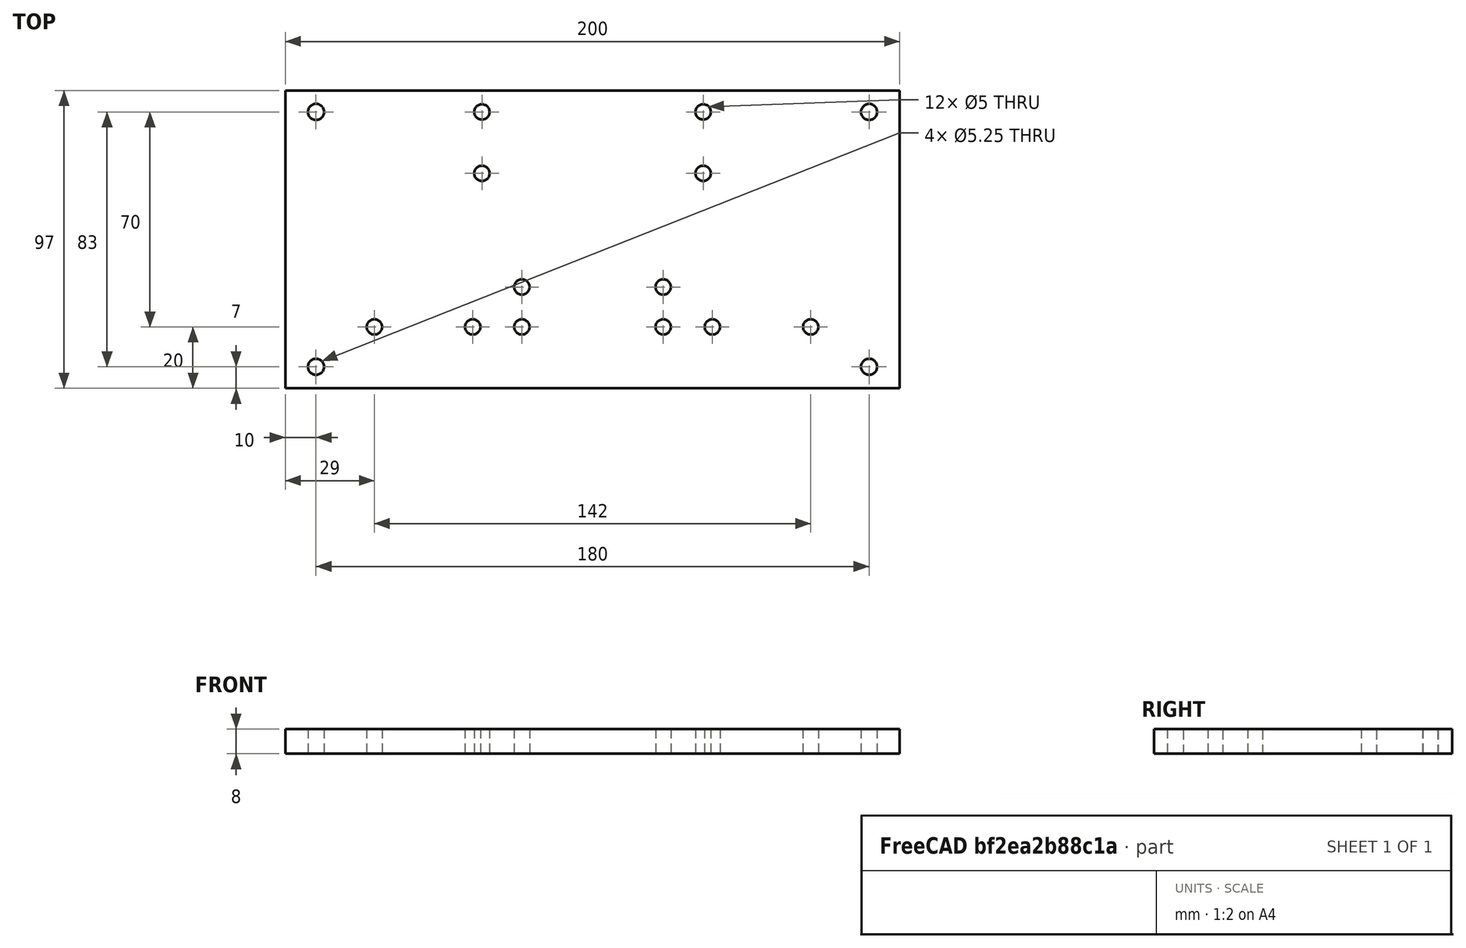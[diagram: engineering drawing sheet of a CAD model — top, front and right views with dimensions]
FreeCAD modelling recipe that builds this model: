
FCSTD DOCUMENT  (FreeCAD 0.15R4671 (Git))
Label: base-right
License: All rights reserved
LicenseURL: http://en.wikipedia.org/wiki/All_rights_reserved
objects: Drawing::FeatureView×27, Drawing::FeatureViewPart×2, Sketcher::SketchObject×1, PartDesign::Pad×1, Drawing::FeaturePage×1
note: 3 computed .brp shape members not serialized (recipe doc carries the construction recipe); baked Part::Feature solids carry a one-line shape summary decoded from their .brp

FEATURE [Sketcher::SketchObject] Sketch  label="main-sketch"
  Placement = pos=(0,0,0) rot=(0,0,1;1.5708rad)
  sketch-geometry (42):
    g0: LineSegment StartX=-48.5 StartY=100 StartZ=0 EndX=48.5 EndY=100 EndZ=0
    g1: LineSegment StartX=48.5 StartY=100 StartZ=0 EndX=48.5 EndY=-100 EndZ=0
    g2: LineSegment StartX=48.5 StartY=-100 StartZ=0 EndX=-48.5 EndY=-100 EndZ=0
    g3: LineSegment StartX=-48.5 StartY=-100 StartZ=0 EndX=-48.5 EndY=100 EndZ=0
    g4: LineSegment [constr] StartX=-28.5 StartY=100 StartZ=0 EndX=-28.5 EndY=-100 EndZ=0
    g5: LineSegment [constr] StartX=-15.5 StartY=23 StartZ=0 EndX=-15.5 EndY=-23 EndZ=0
    g6: LineSegment [constr] StartX=-28.5 StartY=23 StartZ=0 EndX=-15.5 EndY=23 EndZ=0
    g7: LineSegment [constr] StartX=-15.5 StartY=-23 StartZ=0 EndX=-28.5 EndY=-23 EndZ=0
    g8: Circle CenterX=-28.5 CenterY=71 CenterZ=0 NormalX=0 NormalY=0 NormalZ=1 Radius=2.5
    g9: Circle CenterX=-28.5 CenterY=39 CenterZ=0 NormalX=0 NormalY=0 NormalZ=1 Radius=2.5
    g10: Circle CenterX=-28.5 CenterY=-39 CenterZ=0 NormalX=0 NormalY=0 NormalZ=1 Radius=2.5
    g11: Circle CenterX=-28.5 CenterY=-71 CenterZ=0 NormalX=0 NormalY=0 NormalZ=1 Radius=2.5
    g12: GeomPoint [constr] X=-28.5 Y=34 Z=0
    g13: GeomPoint [constr] X=-28.5 Y=30 Z=0
    g14: Circle CenterX=-28.5 CenterY=23 CenterZ=0 NormalX=0 NormalY=0 NormalZ=1 Radius=2.5
    g15: Circle CenterX=-15.5 CenterY=23 CenterZ=0 NormalX=0 NormalY=0 NormalZ=1 Radius=2.5
    g16: Circle CenterX=-28.5 CenterY=-23 CenterZ=0 NormalX=0 NormalY=0 NormalZ=1 Radius=2.5
    g17: Circle CenterX=-15.5 CenterY=-23 CenterZ=0 NormalX=0 NormalY=0 NormalZ=1 Radius=2.5
    g18: LineSegment [constr] StartX=-41.5 StartY=90 StartZ=0 EndX=41.5 EndY=90 EndZ=0
    g19: LineSegment [constr] StartX=41.5 StartY=90 StartZ=0 EndX=41.5 EndY=-90 EndZ=0
    g20: LineSegment [constr] StartX=41.5 StartY=-90 StartZ=0 EndX=-41.5 EndY=-90 EndZ=0
    g21: LineSegment [constr] StartX=-41.5 StartY=-90 StartZ=0 EndX=-41.5 EndY=90 EndZ=0
    g22: Circle CenterX=-41.5 CenterY=90 CenterZ=0 NormalX=0 NormalY=0 NormalZ=1 Radius=2.625
    g23: Circle CenterX=41.5 CenterY=90 CenterZ=0 NormalX=0 NormalY=0 NormalZ=1 Radius=2.625
    g24: Circle CenterX=-41.5 CenterY=-90 CenterZ=0 NormalX=0 NormalY=0 NormalZ=1 Radius=2.625
    g25: Circle CenterX=41.5 CenterY=-90 CenterZ=0 NormalX=0 NormalY=0 NormalZ=1 Radius=2.625
    g26: GeomPoint [constr] X=18.5 Y=0 Z=0
    g27: GeomPoint [constr] X=22.5 Y=0 Z=0
    g28: GeomPoint [constr] X=46.5 Y=0 Z=0
    g29: GeomPoint [constr] X=41.5 Y=0 Z=0
    g30: LineSegment [constr] StartX=21.5 StartY=36 StartZ=0 EndX=41.5 EndY=36 EndZ=0
    g31: LineSegment [constr] StartX=41.5 StartY=36 StartZ=0 EndX=41.5 EndY=-36 EndZ=0
    g32: LineSegment [constr] StartX=41.5 StartY=-36 StartZ=0 EndX=21.5 EndY=-36 EndZ=0
    g33: LineSegment [constr] StartX=21.5 StartY=-36 StartZ=0 EndX=21.5 EndY=36 EndZ=0
    g34: Circle CenterX=21.5 CenterY=36 CenterZ=0 NormalX=0 NormalY=0 NormalZ=1 Radius=2.5
    g35: Circle CenterX=41.5 CenterY=36 CenterZ=0 NormalX=0 NormalY=0 NormalZ=1 Radius=2.5
    g36: Circle CenterX=21.5 CenterY=-36 CenterZ=0 NormalX=0 NormalY=0 NormalZ=1 Radius=2.5
    g37: Circle CenterX=41.5 CenterY=-36 CenterZ=0 NormalX=0 NormalY=0 NormalZ=1 Radius=2.5
    g38: GeomPoint [constr] X=-35.5 Y=0 Z=0
    g39: GeomPoint [constr] X=-28.5 Y=0 Z=0
    g40: GeomPoint [constr] X=-28.5 Y=55 Z=0
    g41: GeomPoint [constr] X=-28.5 Y=-55 Z=0
  constraints (103):
    c: Coincident(g0,g1)
    c: Coincident(g1,g2)
    c: Coincident(g2,g3)
    c: Coincident(g3,g0)
    c: Horizontal(g0)
    c: Horizontal(g2)
    c: Vertical(g1)
    c: Vertical(g3)
    c: DistanceY(g0,g1) = -200
    c: Symmetric(g0,g1,g-1)
    c: Symmetric(g4,g4,g-1)
    c: Vertical(g5)
    c: Symmetric(g5,g5,g-1)
    c: PointOnObject(g6,g4)
    c: Coincident(g6,g5)
    c: Horizontal(g6)
    c: Coincident(g7,g5)
    c: PointOnObject(g7,g4)
    c: Horizontal(g7)
    c: DistanceX(g7,g5) = 13
    c: DistanceY(g5,g5) = -46
    c: DistanceX(g2,g4) = 20
    c: PointOnObject(g8,g4)
    c: PointOnObject(g11,g4)
    c: Radius(g10) = 2.5
    c: Equal(g10,g11)
    c: Equal(g10,g9)
    c: Equal(g10,g8)
    c: DistanceY(g8,g9) = -32
    c: DistanceY(g10,g11) = -32
    c: Symmetric(g9,g10,g-1)
    c: PointOnObject(g4,g0)
    c: PointOnObject(g12,g4)
    c: DistanceY(g9,g12) = -5
    c: PointOnObject(g13,g4)
    c: DistanceY(g13,g6) = -7
    c: DistanceY(g12,g13) = -4
    c: Coincident(g14,g6)
    c: Coincident(g15,g5)
    c: Coincident(g16,g7)
    c: Coincident(g17,g5)
    c: Radius(g14) = 2.5
    c: Equal(g14,g15)
    c: Equal(g14,g17)
    c: Equal(g14,g16)
    c: Coincident(g18,g19)
    c: Coincident(g19,g20)
    c: Coincident(g20,g21)
    c: Coincident(g21,g18)
    c: Horizontal(g18)
    c: Horizontal(g20)
    c: Vertical(g19)
    c: Vertical(g21)
    c: DistanceX(g18,g0) = -7
    c: DistanceY(g18,g0) = 10
    c: Symmetric(g0,g0,g-2)
    c: Symmetric(g18,g18,g-2)
    c: Symmetric(g18,g19,g-1)
    c: Coincident(g22,g18)
    c: Coincident(g23,g18)
    c: Coincident(g24,g20)
    c: Coincident(g25,g19)
    c: Radius(g25) = 2.625
    c: Equal(g25,g24)
    c: Equal(g25,g22)
    c: Equal(g25,g23)
    c: PointOnObject(g26,g-1)
    c: PointOnObject(g27,g-1)
    c: DistanceX(g26,g27) = 4
    c: PointOnObject(g28,g-1)
    c: DistanceX(g27,g28) = 24
    c: PointOnObject(g29,g-1)
    c: DistanceX(g29,g28) = 5
    c: Coincident(g30,g31)
    c: Coincident(g31,g32)
    c: Coincident(g32,g33)
    c: Coincident(g33,g30)
    c: Horizontal(g30)
    c: Horizontal(g32)
    c: Vertical(g31)
    c: Vertical(g33)
    c: PointOnObject(g29,g31)
    c: DistanceX(g30,g30) = -20
    c: DistanceY(g30,g31) = -72
    c: Symmetric(g30,g32,g-1)
    c: Coincident(g34,g30)
    c: Coincident(g35,g30)
    c: Coincident(g36,g32)
    c: Coincident(g37,g31)
    c: Radius(g37) = 2.5
    c: Equal(g37,g36)
    c: Equal(g37,g34)
    c: Equal(g37,g35)
    c: PointOnObject(g31,g19)
    c: PointOnObject(g38,g-1)
    c: PointOnObject(g39,g4)
    c: PointOnObject(g39,g-1)
    c: DistanceX(g38,g39) = 7
    c: DistanceX(g26,g38) = -54
    c: PointOnObject(g40,g4)
    c: Symmetric(g8,g9,g40)
    c: PointOnObject(g41,g4)
    c: Symmetric(g10,g11,g41)
FEATURE [PartDesign::Pad] Pad  label="base-right"
  Length = 8
  Length2 = 100
  Placement = pos=(0,0,0) rot=(0,0,1;1.5708rad)
  Sketch = -> Sketch
  Type = 0
FEATURE [Drawing::FeatureViewPart] Ortho  label="Ortho_0_0"
  Direction = (0,0,1)
  HiddenWidth = 0.15
  LineWidth = 0.35
  Rotation = 0
  ShowHiddenLines = false
  ShowSmoothLines = false
  Source = -> Pad
  Tolerance = 0.05
  ViewResult = <g id="Ortho_0_0"\n   transform="rotate(0,148.5,84.1667) translate(148.5,84.1667) scale(1,1)"\n  >\n<g   stroke="rgb(0, 0, 0)"\n   stroke-width="0.35"\n   stroke-linecap="butt"\n   stroke-linejoin="miter"\n   fill="none"\n   transform="scale(1,-1)"\n  >\n<path id= "1" d=" M -100 -48.5 L -100 48.5 " />\n<path id= "2" d=" M -100 48.5 L 100 48.5 " />\n<path id= "3" d=" M 100 48.5 L 100 -48.5 " />\n<path id= "4" d=" M 100 -48.5 L -100 -48.5 " />\n<circle cx ="90" cy ="41.5" r ="2.625" /><circle cx ="90" cy ="-41.5" r ="2.625" /><circle cx ="-90" cy ="41.5" r ="2.625" /><circle cx ="-90" cy ="-41.5" r ="2.625" /><circle cx ="36" cy ="41.5" r ="2.5" /><circle cx ="-36" cy ="41.5" r ="2.5" /><circle cx ="-39" cy ="-28.5" r ="2.5" /><circle cx ="39" cy ="-28.5" r ="2.5" /><circle cx ="71" cy ="-28.5" r ="2.5" /><circle cx ="-36" cy ="21.5" r ="2.5" /><circle cx ="36" cy ="21.5" r ="2.5" /><circle cx ="-71" cy ="-28.5" r ="2.5" /><circle cx ="-23" cy ="-15.5" r ="2.5" /><circle cx ="23" cy ="-15.5" r ="2.5" /><circle cx ="-23" cy ="-28.5" r ="2.5" /><circle cx ="23" cy ="-28.5" r ="2.5" /></g>\n</g>
  Visible = true
  X = 148.5
  Y = 84.1667
FEATURE [Drawing::FeatureViewPart] Ortho001  label="Ortho_0_-1"
  Direction = (0,-1,0)
  HiddenWidth = 0.15
  LineWidth = 0.35
  Rotation = 90
  ShowHiddenLines = false
  ShowSmoothLines = false
  Source = -> Pad
  Tolerance = 0.05
  ViewResult = <g id="Ortho_0_-1"\n   transform="rotate(90,148.5,174.333) translate(148.5,174.333) scale(1,1)"\n  >\n<g   stroke="rgb(0, 0, 0)"\n   stroke-width="0.35"\n   stroke-linecap="butt"\n   stroke-linejoin="miter"\n   fill="none"\n   transform="scale(1,-1)"\n  >\n<path id= "1" d=" M 0 -100 L -8 -100 " />\n<path id= "2" d=" M 0 100 L -8 100 " />\n<path id= "3" d=" M 0 100 L 0 -100 " />\n<path id= "4" d=" M -8 100 L -8 -100 " />\n</g>\n</g>
  Visible = true
  X = 148.5
  Y = 174.333
FEATURE [Drawing::FeatureView] dim001
  Rotation = 0
  ViewResult = <g> \n  <line x1="46.500000" y1="35.666700" x2="20.569600" y2="35.666700" style="stroke:rgb(0,0,255);stroke-width:0.50" />\n<line x1="46.500000" y1="132.666700" x2="20.569600" y2="132.666700" style="stroke:rgb(0,0,255);stroke-width:0.50" />\n<line x1="21.569600" y1="35.666700" x2="21.569600" y2="132.666700" style="stroke:rgb(0,0,255);stroke-width:0.50" /> \n  <polygon points="21.569600,132.666700 22.569600,129.666700 21.569600,128.666700 20.569600,129.666700" style="fill:rgb(0,0,255);stroke:rgb(0,0,255);stroke-width:0" /><polygon points="21.569600,35.666700 20.569600,38.666700 21.569600,39.666700 22.569600,38.666700" style="fill:rgb(0,0,255);stroke:rgb(0,0,255);stroke-width:0" /> \n  <text x="19.569600" y="84.166700" font-family="inherit" font-size="3.6" fill="rgb(0,0,255)" text-anchor="middle" transform="rotate(-90.000000 19.569600,84.166700)" >97</text> </g>
  Visible = true
  X = 0
  Y = 0
FEATURE [Drawing::FeatureView] dim002
  Rotation = 0
  ViewResult = <g> \n  <line x1="56.500000" y1="42.666700" x2="30.059043" y2="42.666700" style="stroke:rgb(0,0,255);stroke-width:0.50" />\n<line x1="56.500000" y1="125.666700" x2="30.059043" y2="125.666700" style="stroke:rgb(0,0,255);stroke-width:0.50" />\n<line x1="31.059043" y1="42.666700" x2="31.059043" y2="125.666700" style="stroke:rgb(0,0,255);stroke-width:0.50" /> \n  <polygon points="31.059043,125.666700 32.059043,122.666700 31.059043,121.666700 30.059043,122.666700" style="fill:rgb(0,0,255);stroke:rgb(0,0,255);stroke-width:0" /><polygon points="31.059043,42.666700 30.059043,45.666700 31.059043,46.666700 32.059043,45.666700" style="fill:rgb(0,0,255);stroke:rgb(0,0,255);stroke-width:0" /> \n  <text x="29.059043" y="84.166700" font-family="inherit" font-size="3.6" fill="rgb(0,0,255)" text-anchor="middle" transform="rotate(-90.000000 29.059043,84.166700)" >83</text> </g>
  Visible = true
  X = 0
  Y = 0
FEATURE [Drawing::FeatureView] dim003
  Rotation = 0
  ViewResult = <g> \n  <line x1="48.500000" y1="33.666700" x2="48.500000" y2="9.255344" style="stroke:rgb(0,0,255);stroke-width:0.50" />\n<line x1="248.500000" y1="33.666700" x2="248.500000" y2="9.255344" style="stroke:rgb(0,0,255);stroke-width:0.50" />\n<line x1="48.500000" y1="10.255344" x2="248.500000" y2="10.255344" style="stroke:rgb(0,0,255);stroke-width:0.50" /> \n  <polygon points="248.500000,10.255344 245.500000,9.255344 244.500000,10.255344 245.500000,11.255344" style="fill:rgb(0,0,255);stroke:rgb(0,0,255);stroke-width:0" /><polygon points="48.500000,10.255344 51.500000,11.255344 52.500000,10.255344 51.500000,9.255344" style="fill:rgb(0,0,255);stroke:rgb(0,0,255);stroke-width:0" /> \n  <text x="148.500000" y="8.255344" font-family="inherit" font-size="3.6" fill="rgb(0,0,255)" text-anchor="middle" transform="rotate(0.000000 148.500000,8.255344)" >200</text> </g>
  Visible = true
  X = 0
  Y = 0
FEATURE [Drawing::FeatureView] dim004
  Rotation = 0
  ViewResult = <g> \n  <line x1="58.500000" y1="40.666700" x2="58.500000" y2="17.873400" style="stroke:rgb(0,0,255);stroke-width:0.50" />\n<line x1="238.500000" y1="40.666700" x2="238.500000" y2="17.873400" style="stroke:rgb(0,0,255);stroke-width:0.50" />\n<line x1="58.500000" y1="18.873400" x2="238.500000" y2="18.873400" style="stroke:rgb(0,0,255);stroke-width:0.50" /> \n  <polygon points="238.500000,18.873400 235.500000,17.873400 234.500000,18.873400 235.500000,19.873400" style="fill:rgb(0,0,255);stroke:rgb(0,0,255);stroke-width:0" /><polygon points="58.500000,18.873400 61.500000,19.873400 62.500000,18.873400 61.500000,17.873400" style="fill:rgb(0,0,255);stroke:rgb(0,0,255);stroke-width:0" /> \n  <text x="148.500000" y="16.873400" font-family="inherit" font-size="3.6" fill="rgb(0,0,255)" text-anchor="middle" transform="rotate(0.000000 148.500000,16.873400)" >180</text> </g>
  Visible = true
  X = 0
  Y = 0
FEATURE [Drawing::FeatureView] dim009
  Rotation = 0
  ViewResult = <g> \n  <line x1="123.500000" y1="99.666700" x2="117.888672" y2="99.666700" style="stroke:rgb(0,0,255);stroke-width:0.50" />\n<line x1="123.500000" y1="112.666700" x2="117.888672" y2="112.666700" style="stroke:rgb(0,0,255);stroke-width:0.50" />\n<line x1="118.888672" y1="99.666700" x2="118.888672" y2="112.666700" style="stroke:rgb(0,0,255);stroke-width:0.50" /> \n  <polygon points="118.888672,112.666700 119.888672,109.666700 118.888672,108.666700 117.888672,109.666700" style="fill:rgb(0,0,255);stroke:rgb(0,0,255);stroke-width:0" /><polygon points="118.888672,99.666700 117.888672,102.666700 118.888672,103.666700 119.888672,102.666700" style="fill:rgb(0,0,255);stroke:rgb(0,0,255);stroke-width:0" /> \n  <text x="116.888672" y="106.166700" font-family="inherit" font-size="3.6" fill="rgb(0,0,255)" text-anchor="middle" transform="rotate(-90.000000 116.888672,106.166700)" >13</text> </g>
  Visible = true
  X = 0
  Y = 0
FEATURE [Drawing::FeatureView] dim012
  Rotation = 0
  ViewResult = <g> \n  <line x1="110.500000" y1="42.666700" x2="92.685148" y2="42.666700" style="stroke:rgb(0,0,255);stroke-width:0.50" />\n<line x1="110.500000" y1="62.666700" x2="92.685148" y2="62.666700" style="stroke:rgb(0,0,255);stroke-width:0.50" />\n<line x1="93.685148" y1="42.666700" x2="93.685148" y2="62.666700" style="stroke:rgb(0,0,255);stroke-width:0.50" /> \n  <polygon points="93.685148,62.666700 94.685148,59.666700 93.685148,58.666700 92.685148,59.666700" style="fill:rgb(0,0,255);stroke:rgb(0,0,255);stroke-width:0" /><polygon points="93.685148,42.666700 92.685148,45.666700 93.685148,46.666700 94.685148,45.666700" style="fill:rgb(0,0,255);stroke:rgb(0,0,255);stroke-width:0" /> \n  <text x="91.685148" y="52.666700" font-family="inherit" font-size="3.6" fill="rgb(0,0,255)" text-anchor="middle" transform="rotate(-90.000000 91.685148,52.666700)" >20</text> </g>
  Visible = true
  X = 0
  Y = 0
FEATURE [Drawing::FeatureView] centerLines001
  Rotation = 0
  ViewResult = <g transform="scale(1.000000,1.000000)" stroke="rgb(0,0,255)"  stroke-width="0.320000" > <path d="M 148.500000,35.666700 L 148.500000,38.666700 M 148.500000,40.666700 L 148.500000,46.666700 M 148.500000,48.666700 L 148.500000,51.666700 M 148.500000,53.666700 L 148.500000,59.666700 M 148.500000,61.666700 L 148.500000,64.666700 M 148.500000,66.666700 L 148.500000,72.666700 M 148.500000,74.666700 L 148.500000,77.666700 M 148.500000,79.666700 L 148.500000,85.666700 M 148.500000,87.666700 L 148.500000,90.666700 M 148.500000,92.666700 L 148.500000,98.666700 M 148.500000,100.666700 L 148.500000,103.666700 M 148.500000,105.666700 L 148.500000,111.666700 M 148.500000,113.666700 L 148.500000,116.666700 M 148.500000,118.666700 L 148.500000,124.666700 M 148.500000,126.666700 L 148.500000,129.666700 M 148.500000,131.666700 L 148.500000,134.315710 "/>\n<path d="M 148.500000,35.666700 L 148.500000,38.666700 M 148.500000,40.666700 L 148.500000,46.666700 M 148.500000,48.666700 L 148.500000,51.666700 M 148.500000,53.666700 L 148.500000,59.666700 M 148.500000,61.666700 L 148.500000,64.666700 M 148.500000,66.666700 L 148.500000,72.666700 M 148.500000,74.666700 L 148.500000,77.666700 M 148.500000,79.666700 L 148.500000,85.666700 M 148.500000,87.666700 L 148.500000,90.666700 M 148.500000,92.666700 L 148.500000,98.666700 M 148.500000,100.666700 L 148.500000,103.666700 M 148.500000,105.666700 L 148.500000,111.666700 M 148.500000,113.666700 L 148.500000,116.666700 M 148.500000,118.666700 L 148.500000,124.666700 M 148.500000,126.666700 L 148.500000,129.666700 M 148.500000,131.666700 L 148.500000,134.315710 "/> </g> 
  Visible = true
  X = 0
  Y = 0
FEATURE [Drawing::FeatureView] dim015
  Rotation = 0
  ViewResult = <g>  <circle cx ="77.500000" cy ="112.666700" r="0.250000" stroke="none" fill="rgb(0,0,255)" /> \n<line x1="81.248488" y1="106.813745" x2="76.151703" y2="114.771954" style="stroke:rgb(0,0,255);stroke-width:0.50" />\n<polygon points="78.848297,110.561446 81.308355,108.574459 81.005572,107.193039 79.624151,107.495822" style="fill:rgb(0,0,255);stroke:rgb(0,0,255);stroke-width:0" />\n<polygon points="76.151703,114.771954 73.691645,116.758941 73.994428,118.140361 75.375849,117.837578" style="fill:rgb(0,0,255);stroke:rgb(0,0,255);stroke-width:0" />\n<line x1="81.248488" y1="106.813745" x2="91.054340" y2="106.813745" style="stroke:rgb(0,0,255);stroke-width:0.50" />\n<text x="86.151414" y="104.813745" font-family="inherit" font-size="3.6" fill="rgb(0,0,255)" text-anchor="middle"  >2 x Ø5</text> </g>
  Visible = true
  X = 0
  Y = 0
FEATURE [Drawing::FeatureView] dim016
  Rotation = 0
  ViewResult = <g>  <circle cx ="187.500000" cy ="112.666700" r="0.250000" stroke="none" fill="rgb(0,0,255)" /> \n<line x1="192.264741" y1="106.113327" x2="186.029843" y2="114.688738" style="stroke:rgb(0,0,255);stroke-width:0.50" />\n<polygon points="188.970157,110.644662 191.543161,108.806279 191.322409,107.409401 189.925530,107.630153" style="fill:rgb(0,0,255);stroke:rgb(0,0,255);stroke-width:0" />\n<polygon points="186.029843,114.688738 183.456839,116.527121 183.677591,117.923999 185.074470,117.703247" style="fill:rgb(0,0,255);stroke:rgb(0,0,255);stroke-width:0" />\n<line x1="192.264741" y1="106.113327" x2="202.771011" y2="106.113327" style="stroke:rgb(0,0,255);stroke-width:0.50" />\n<text x="197.517876" y="104.113327" font-family="inherit" font-size="3.6" fill="rgb(0,0,255)" text-anchor="middle"  >2 x Ø5</text> </g>
  Visible = true
  X = 0
  Y = 0
FEATURE [Drawing::FeatureView] dim017
  Rotation = 0
  ViewResult = <g>  <circle cx ="125.500000" cy ="112.666700" r="0.250000" stroke="none" fill="rgb(0,0,255)" /> \n<line x1="129.227121" y1="106.813745" x2="124.157167" y2="114.775443" style="stroke:rgb(0,0,255);stroke-width:0.50" />\n<polygon points="126.842833,110.557957 129.297730,108.564598 128.991366,107.183967 127.610736,107.490331" style="fill:rgb(0,0,255);stroke:rgb(0,0,255);stroke-width:0" />\n<polygon points="124.157167,114.775443 121.702270,116.768802 122.008634,118.149433 123.389264,117.843069" style="fill:rgb(0,0,255);stroke:rgb(0,0,255);stroke-width:0" />\n<line x1="129.227121" y1="106.813745" x2="141.484436" y2="106.813745" style="stroke:rgb(0,0,255);stroke-width:0.50" />\n<text x="135.355779" y="104.813745" font-family="inherit" font-size="3.6" fill="rgb(0,0,255)" text-anchor="middle"  >4 x Ø5</text> </g>
  Visible = true
  X = 0
  Y = 0
FEATURE [Drawing::FeatureView] dim018
  Rotation = 0
  ViewResult = <g>  <circle cx ="112.500000" cy ="62.666700" r="0.250000" stroke="none" fill="rgb(0,0,255)" /> \n<line x1="115.919179" y1="56.733858" x2="111.251684" y2="64.832735" style="stroke:rgb(0,0,255);stroke-width:0.50" />\n<polygon points="113.748316,60.500665 116.112709,58.400750 115.745621,57.035009 114.379881,57.402097" style="fill:rgb(0,0,255);stroke:rgb(0,0,255);stroke-width:0" />\n<polygon points="111.251684,64.832735 108.887291,66.932650 109.254379,68.298391 110.620119,67.931303" style="fill:rgb(0,0,255);stroke:rgb(0,0,255);stroke-width:0" />\n<line x1="115.919179" y1="56.733858" x2="127.125867" y2="56.733858" style="stroke:rgb(0,0,255);stroke-width:0.50" />\n<text x="121.522523" y="54.733858" font-family="inherit" font-size="3.6" fill="rgb(0,0,255)" text-anchor="middle"  >4 x Ø5</text> </g>
  Visible = true
  X = 0
  Y = 0
FEATURE [Drawing::FeatureView] centerLines002
  Rotation = 0
  ViewResult = <blob: 3032 chars omitted>
  Visible = true
  X = 0
  Y = 0
FEATURE [Drawing::FeatureView] dim005
  Rotation = 0
  ViewResult = <g> \n  <line x1="46.500000" y1="166.333000" x2="33.031552" y2="166.333000" style="stroke:rgb(0,0,255);stroke-width:0.50" />\n<line x1="46.500000" y1="174.333000" x2="33.031552" y2="174.333000" style="stroke:rgb(0,0,255);stroke-width:0.50" />\n<line x1="34.031552" y1="166.333000" x2="34.031552" y2="174.333000" style="stroke:rgb(0,0,255);stroke-width:0.50" /> \n  <polygon points="34.031552,174.333000 33.031552,177.333000 34.031552,178.333000 35.031552,177.333000" style="fill:rgb(0,0,255);stroke:rgb(0,0,255);stroke-width:0" /><polygon points="34.031552,166.333000 35.031552,163.333000 34.031552,162.333000 33.031552,163.333000" style="fill:rgb(0,0,255);stroke:rgb(0,0,255);stroke-width:0" /> \n  <text x="32.031552" y="170.333000" font-family="inherit" font-size="3.6" fill="rgb(0,0,255)" text-anchor="middle" transform="rotate(-90.000000 32.031552,170.333000)" >8</text> </g>
  Visible = true
  X = 0
  Y = 0
FEATURE [Drawing::FeatureView] dim019
  Rotation = 0
  ViewResult = <g> \n  <line x1="56.500000" y1="125.666700" x2="30.064229" y2="125.666700" style="stroke:rgb(0,0,255);stroke-width:0.50" />\n<line x1="46.500000" y1="132.666700" x2="30.064229" y2="132.666700" style="stroke:rgb(0,0,255);stroke-width:0.50" />\n<line x1="31.064229" y1="125.666700" x2="31.064229" y2="132.666700" style="stroke:rgb(0,0,255);stroke-width:0.50" /> \n  <polygon points="31.064229,132.666700 30.064229,135.666700 31.064229,136.666700 32.064229,135.666700" style="fill:rgb(0,0,255);stroke:rgb(0,0,255);stroke-width:0" /><polygon points="31.064229,125.666700 32.064229,122.666700 31.064229,121.666700 30.064229,122.666700" style="fill:rgb(0,0,255);stroke:rgb(0,0,255);stroke-width:0" /> \n  <text x="29.064229" y="129.166700" font-family="inherit" font-size="3.6" fill="rgb(0,0,255)" text-anchor="middle" transform="rotate(-90.000000 29.064229,129.166700)" >7</text> </g>
  Visible = true
  X = 0
  Y = 0
FEATURE [Drawing::FeatureView] dim020
  Rotation = 0
  ViewResult = <g> \n  <line x1="58.500000" y1="40.666700" x2="58.500000" y2="17.905088" style="stroke:rgb(0,0,255);stroke-width:0.50" />\n<line x1="48.500000" y1="33.666700" x2="48.500000" y2="17.905088" style="stroke:rgb(0,0,255);stroke-width:0.50" />\n<line x1="58.500000" y1="18.905088" x2="48.500000" y2="18.905088" style="stroke:rgb(0,0,255);stroke-width:0.50" /> \n  <polygon points="48.500000,18.905088 45.500000,17.905088 44.500000,18.905088 45.500000,19.905088" style="fill:rgb(0,0,255);stroke:rgb(0,0,255);stroke-width:0" /><polygon points="58.500000,18.905088 61.500000,19.905088 62.500000,18.905088 61.500000,17.905088" style="fill:rgb(0,0,255);stroke:rgb(0,0,255);stroke-width:0" /> \n  <text x="53.500000" y="16.905088" font-family="inherit" font-size="3.6" fill="rgb(0,0,255)" text-anchor="middle" transform="rotate(0.000000 53.500000,16.905088)" >10</text> </g>
  Visible = true
  X = 0
  Y = 0
FEATURE [Drawing::FeatureView] dim022
  Rotation = 0
  ViewResult = <g> \n  <line x1="110.500000" y1="42.666700" x2="92.702372" y2="42.666700" style="stroke:rgb(0,0,255);stroke-width:0.50" />\n<line x1="246.500000" y1="35.666700" x2="92.702372" y2="35.666700" style="stroke:rgb(0,0,255);stroke-width:0.50" />\n<line x1="93.702372" y1="42.666700" x2="93.702372" y2="35.666700" style="stroke:rgb(0,0,255);stroke-width:0.50" /> \n  <polygon points="93.702372,35.666700 94.702372,32.666700 93.702372,31.666700 92.702372,32.666700" style="fill:rgb(0,0,255);stroke:rgb(0,0,255);stroke-width:0" /><polygon points="93.702372,42.666700 92.702372,45.666700 93.702372,46.666700 94.702372,45.666700" style="fill:rgb(0,0,255);stroke:rgb(0,0,255);stroke-width:0" /> \n  <text x="91.702372" y="39.166700" font-family="inherit" font-size="3.6" fill="rgb(0,0,255)" text-anchor="middle" transform="rotate(-90.000000 91.702372,39.166700)" >7</text> </g>
  Visible = true
  X = 0
  Y = 0
FEATURE [Drawing::FeatureView] dim007
  Rotation = 0
  ViewResult = <g> \n  <line x1="77.500000" y1="114.666700" x2="77.500000" y2="143.575869" style="stroke:rgb(0,0,255);stroke-width:0.50" />\n<line x1="109.500000" y1="114.666700" x2="109.500000" y2="143.575869" style="stroke:rgb(0,0,255);stroke-width:0.50" />\n<line x1="77.500000" y1="142.575869" x2="109.500000" y2="142.575869" style="stroke:rgb(0,0,255);stroke-width:0.50" /> \n  <polygon points="109.500000,142.575869 106.500000,141.575869 105.500000,142.575869 106.500000,143.575869" style="fill:rgb(0,0,255);stroke:rgb(0,0,255);stroke-width:0" /><polygon points="77.500000,142.575869 80.500000,143.575869 81.500000,142.575869 80.500000,141.575869" style="fill:rgb(0,0,255);stroke:rgb(0,0,255);stroke-width:0" /> \n  <text x="93.500000" y="140.575869" font-family="inherit" font-size="3.6" fill="rgb(0,0,255)" text-anchor="middle" transform="rotate(0.000000 93.500000,140.575869)" >32</text> </g>
  Visible = true
  X = 0
  Y = 0
FEATURE [Drawing::FeatureView] dim008
  Rotation = 0
  ViewResult = <g> \n  <line x1="187.500000" y1="114.666700" x2="187.500000" y2="143.274168" style="stroke:rgb(0,0,255);stroke-width:0.50" />\n<line x1="219.500000" y1="114.666700" x2="219.500000" y2="143.274168" style="stroke:rgb(0,0,255);stroke-width:0.50" />\n<line x1="187.500000" y1="142.274168" x2="219.500000" y2="142.274168" style="stroke:rgb(0,0,255);stroke-width:0.50" /> \n  <polygon points="219.500000,142.274168 216.500000,141.274168 215.500000,142.274168 216.500000,143.274168" style="fill:rgb(0,0,255);stroke:rgb(0,0,255);stroke-width:0" /><polygon points="187.500000,142.274168 190.500000,143.274168 191.500000,142.274168 190.500000,141.274168" style="fill:rgb(0,0,255);stroke:rgb(0,0,255);stroke-width:0" /> \n  <text x="203.500000" y="140.274168" font-family="inherit" font-size="3.6" fill="rgb(0,0,255)" text-anchor="middle" transform="rotate(0.000000 203.500000,140.274168)" >32</text> </g>
  Visible = true
  X = 0
  Y = 0
FEATURE [Drawing::FeatureView] dim024
  Rotation = 0
  ViewResult = <g> \n  <line x1="123.500000" y1="112.666700" x2="117.910261" y2="112.666700" style="stroke:rgb(0,0,255);stroke-width:0.50" />\n<line x1="246.500000" y1="132.666700" x2="117.910261" y2="132.666700" style="stroke:rgb(0,0,255);stroke-width:0.50" />\n<line x1="118.910261" y1="112.666700" x2="118.910261" y2="132.666700" style="stroke:rgb(0,0,255);stroke-width:0.50" /> \n  <polygon points="118.910261,132.666700 119.910261,129.666700 118.910261,128.666700 117.910261,129.666700" style="fill:rgb(0,0,255);stroke:rgb(0,0,255);stroke-width:0" /><polygon points="118.910261,112.666700 117.910261,115.666700 118.910261,116.666700 119.910261,115.666700" style="fill:rgb(0,0,255);stroke:rgb(0,0,255);stroke-width:0" /> \n  <text x="116.910261" y="122.666700" font-family="inherit" font-size="3.6" fill="rgb(0,0,255)" text-anchor="middle" transform="rotate(-90.000000 116.910261,122.666700)" >20</text> </g>
  Visible = true
  X = 0
  Y = 0
FEATURE [Drawing::FeatureView] dim014
  Rotation = 0
  ViewResult = <g>  <circle cx ="58.500000" cy ="42.666700" r="0.250000" stroke="none" fill="rgb(0,0,255)" /> \n<line x1="62.128458" y1="53.741116" x2="57.682688" y2="40.172181" style="stroke:rgb(0,0,255);stroke-width:0.50" />\n<polygon points="59.317312,45.161219 59.301091,48.323455 60.562741,48.962391 61.201677,47.700741" style="fill:rgb(0,0,255);stroke:rgb(0,0,255);stroke-width:0" />\n<polygon points="57.682688,40.172181 57.698909,37.009945 56.437259,36.371009 55.798323,37.632659" style="fill:rgb(0,0,255);stroke:rgb(0,0,255);stroke-width:0" />\n<line x1="62.128458" y1="53.741116" x2="80.766995" y2="53.741116" style="stroke:rgb(0,0,255);stroke-width:0.50" />\n<text x="71.447726" y="51.741116" font-family="inherit" font-size="3.6" fill="rgb(0,0,255)" text-anchor="middle"  >4 x Ø5.25</text> </g>
  Visible = true
  X = 0
  Y = 0
FEATURE [Drawing::FeatureView] dim011
  Rotation = 0
  ViewResult = <g> \n  <line x1="58.500000" y1="40.666700" x2="58.500000" y2="26.396924" style="stroke:rgb(0,0,255);stroke-width:0.50" />\n<line x1="112.500000" y1="40.666700" x2="112.500000" y2="26.396924" style="stroke:rgb(0,0,255);stroke-width:0.50" />\n<line x1="58.500000" y1="27.396924" x2="112.500000" y2="27.396924" style="stroke:rgb(0,0,255);stroke-width:0.50" /> \n  <polygon points="112.500000,27.396924 109.500000,26.396924 108.500000,27.396924 109.500000,28.396924" style="fill:rgb(0,0,255);stroke:rgb(0,0,255);stroke-width:0" /><polygon points="58.500000,27.396924 61.500000,28.396924 62.500000,27.396924 61.500000,26.396924" style="fill:rgb(0,0,255);stroke:rgb(0,0,255);stroke-width:0" /> \n  <text x="85.500000" y="25.396924" font-family="inherit" font-size="3.6" fill="rgb(0,0,255)" text-anchor="middle" transform="rotate(0.000000 85.500000,25.396924)" >54</text> </g>
  Visible = true
  X = 0
  Y = 0
FEATURE [Drawing::FeatureView] dim021
  Rotation = 0
  ViewResult = <g> \n  <line x1="112.500000" y1="40.666700" x2="112.500000" y2="26.351111" style="stroke:rgb(0,0,255);stroke-width:0.50" />\n<line x1="184.500000" y1="40.666700" x2="184.500000" y2="26.351111" style="stroke:rgb(0,0,255);stroke-width:0.50" />\n<line x1="112.500000" y1="27.351111" x2="184.500000" y2="27.351111" style="stroke:rgb(0,0,255);stroke-width:0.50" /> \n  <polygon points="184.500000,27.351111 181.500000,26.351111 180.500000,27.351111 181.500000,28.351111" style="fill:rgb(0,0,255);stroke:rgb(0,0,255);stroke-width:0" /><polygon points="112.500000,27.351111 115.500000,28.351111 116.500000,27.351111 115.500000,26.351111" style="fill:rgb(0,0,255);stroke:rgb(0,0,255);stroke-width:0" /> \n  <text x="148.500000" y="25.351111" font-family="inherit" font-size="3.6" fill="rgb(0,0,255)" text-anchor="middle" transform="rotate(0.000000 148.500000,25.351111)" >72</text> </g>
  Visible = true
  X = 0
  Y = 0
FEATURE [Drawing::FeatureView] dim023
  Rotation = 0
  ViewResult = <g> \n  <line x1="77.500000" y1="114.666700" x2="77.500000" y2="151.744504" style="stroke:rgb(0,0,255);stroke-width:0.50" />\n<line x1="125.500000" y1="114.666700" x2="125.500000" y2="151.744504" style="stroke:rgb(0,0,255);stroke-width:0.50" />\n<line x1="77.500000" y1="150.744504" x2="125.500000" y2="150.744504" style="stroke:rgb(0,0,255);stroke-width:0.50" /> \n  <polygon points="125.500000,150.744504 122.500000,149.744504 121.500000,150.744504 122.500000,151.744504" style="fill:rgb(0,0,255);stroke:rgb(0,0,255);stroke-width:0" /><polygon points="77.500000,150.744504 80.500000,151.744504 81.500000,150.744504 80.500000,149.744504" style="fill:rgb(0,0,255);stroke:rgb(0,0,255);stroke-width:0" /> \n  <text x="101.500000" y="148.744504" font-family="inherit" font-size="3.6" fill="rgb(0,0,255)" text-anchor="middle" transform="rotate(0.000000 101.500000,148.744504)" >48</text> </g>
  Visible = true
  X = 0
  Y = 0
FEATURE [Drawing::FeatureView] dim010
  Rotation = 0
  ViewResult = <g> \n  <line x1="125.500000" y1="114.666700" x2="125.500000" y2="151.810985" style="stroke:rgb(0,0,255);stroke-width:0.50" />\n<line x1="171.500000" y1="114.666700" x2="171.500000" y2="151.810985" style="stroke:rgb(0,0,255);stroke-width:0.50" />\n<line x1="125.500000" y1="150.810985" x2="171.500000" y2="150.810985" style="stroke:rgb(0,0,255);stroke-width:0.50" /> \n  <polygon points="171.500000,150.810985 168.500000,149.810985 167.500000,150.810985 168.500000,151.810985" style="fill:rgb(0,0,255);stroke:rgb(0,0,255);stroke-width:0" /><polygon points="125.500000,150.810985 128.500000,151.810985 129.500000,150.810985 128.500000,149.810985" style="fill:rgb(0,0,255);stroke:rgb(0,0,255);stroke-width:0" /> \n  <text x="148.500000" y="148.810985" font-family="inherit" font-size="3.6" fill="rgb(0,0,255)" text-anchor="middle" transform="rotate(0.000000 148.500000,148.810985)" >46</text> </g>
  Visible = true
  X = 0
  Y = 0
FEATURE [Drawing::FeatureView] dim025
  Rotation = 0
  ViewResult = <g> \n  <line x1="77.500000" y1="114.666700" x2="77.500000" y2="159.988449" style="stroke:rgb(0,0,255);stroke-width:0.50" />\n<line x1="219.500000" y1="114.666700" x2="219.500000" y2="159.988449" style="stroke:rgb(0,0,255);stroke-width:0.50" />\n<line x1="77.500000" y1="158.988449" x2="219.500000" y2="158.988449" style="stroke:rgb(0,0,255);stroke-width:0.50" /> \n  <polygon points="219.500000,158.988449 216.500000,157.988449 215.500000,158.988449 216.500000,159.988449" style="fill:rgb(0,0,255);stroke:rgb(0,0,255);stroke-width:0" /><polygon points="77.500000,158.988449 80.500000,159.988449 81.500000,158.988449 80.500000,157.988449" style="fill:rgb(0,0,255);stroke:rgb(0,0,255);stroke-width:0" /> \n  <text x="148.500000" y="156.988449" font-family="inherit" font-size="3.6" fill="rgb(0,0,255)" text-anchor="middle" transform="rotate(0.000000 148.500000,156.988449)" >142</text> </g>
  Visible = true
  X = 0
  Y = 0
FEATURE [Drawing::FeatureView] dim006
  Rotation = 0
  ViewResult = <g> \n  <line x1="48.500000" y1="134.666700" x2="48.500000" y2="160.039050" style="stroke:rgb(0,0,255);stroke-width:0.50" />\n<line x1="77.500000" y1="114.666700" x2="77.500000" y2="160.039050" style="stroke:rgb(0,0,255);stroke-width:0.50" />\n<line x1="48.500000" y1="159.039050" x2="77.500000" y2="159.039050" style="stroke:rgb(0,0,255);stroke-width:0.50" /> \n  <polygon points="77.500000,159.039050 74.500000,158.039050 73.500000,159.039050 74.500000,160.039050" style="fill:rgb(0,0,255);stroke:rgb(0,0,255);stroke-width:0" /><polygon points="48.500000,159.039050 51.500000,160.039050 52.500000,159.039050 51.500000,158.039050" style="fill:rgb(0,0,255);stroke:rgb(0,0,255);stroke-width:0" /> \n  <text x="63.000000" y="157.039050" font-family="inherit" font-size="3.6" fill="rgb(0,0,255)" text-anchor="middle" transform="rotate(0.000000 63.000000,157.039050)" >29</text> </g>
  Visible = true
  X = 0
  Y = 0
FEATURE [Drawing::FeatureView] dim026
  Rotation = 0
  ViewResult = <g> \n  <line x1="75.500000" y1="112.666700" x2="67.432479" y2="112.666700" style="stroke:rgb(0,0,255);stroke-width:0.50" />\n<line x1="246.500000" y1="132.666700" x2="67.432479" y2="132.666700" style="stroke:rgb(0,0,255);stroke-width:0.50" />\n<line x1="68.432479" y1="112.666700" x2="68.432479" y2="132.666700" style="stroke:rgb(0,0,255);stroke-width:0.50" /> \n  <polygon points="68.432479,132.666700 69.432479,129.666700 68.432479,128.666700 67.432479,129.666700" style="fill:rgb(0,0,255);stroke:rgb(0,0,255);stroke-width:0" /><polygon points="68.432479,112.666700 67.432479,115.666700 68.432479,116.666700 69.432479,115.666700" style="fill:rgb(0,0,255);stroke:rgb(0,0,255);stroke-width:0" /> \n  <text x="66.432479" y="122.666700" font-family="inherit" font-size="3.6" fill="rgb(0,0,255)" text-anchor="middle" transform="rotate(-90.000000 66.432479,122.666700)" >20</text> </g>
  Visible = true
  X = 0
  Y = 0
FEATURE [Drawing::FeaturePage] Page
  Group = -> [Ortho,Ortho001,dim001,dim002,dim003,dim004,dim009,dim012,centerLines001,dim015,dim016,dim017,dim018,centerLines002,dim005,dim019,dim020,dim022,dim007,dim008,dim024,dim014,dim011,dim021,dim023,dim010,dim025,dim006,dim026]
  Template = <path>
note: 1 file-system path scrubbed to <path> (originals preserved in the JSON sidecar)
